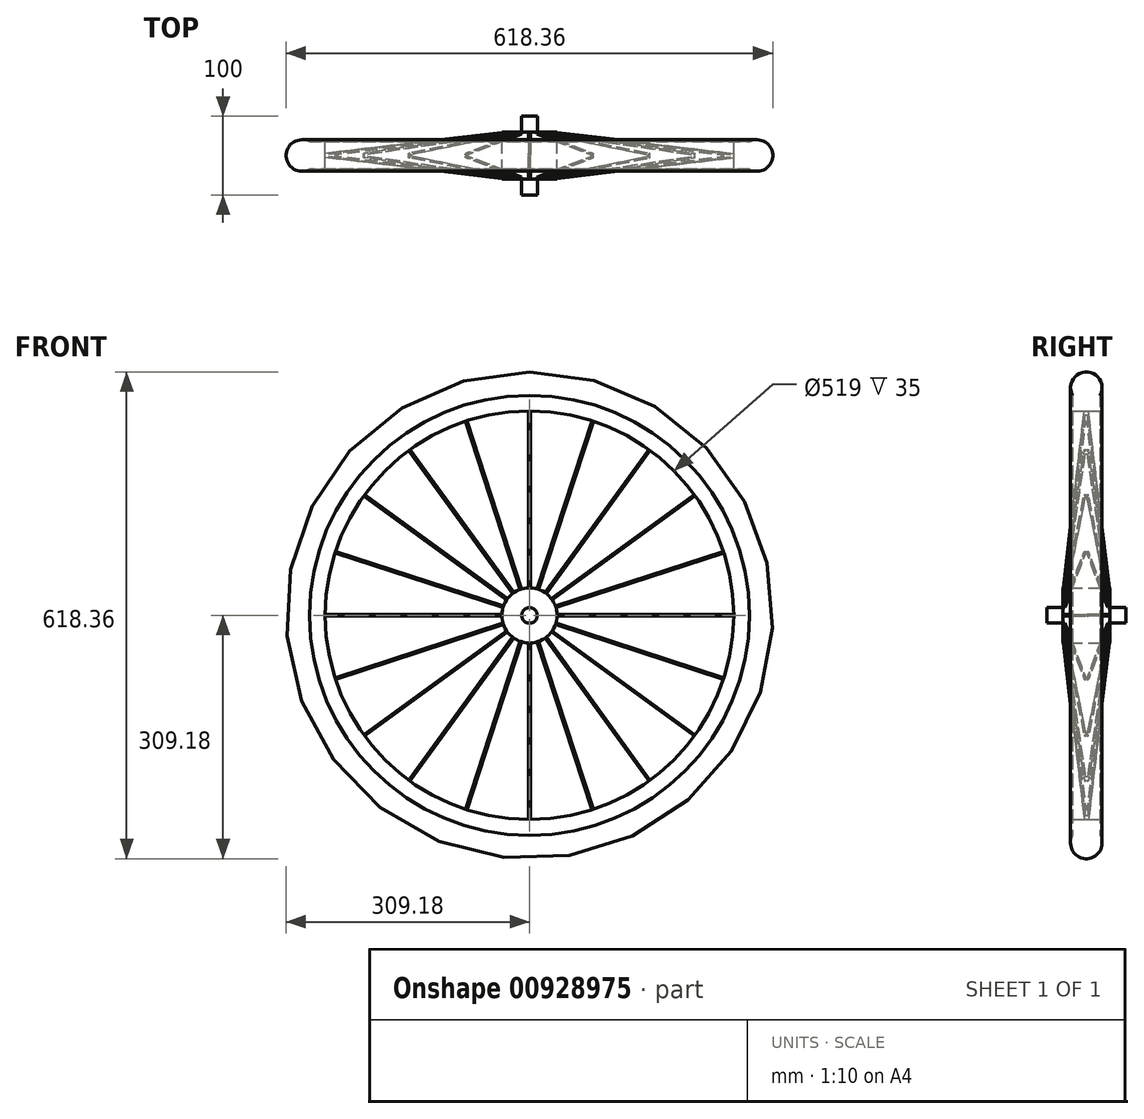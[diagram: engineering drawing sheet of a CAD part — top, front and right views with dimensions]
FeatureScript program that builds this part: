
annotation { "Feature Type Name" : "Feature", "Feature Type Description" : "" }
export const myFeature = defineFeature(function(context is Context, id is Id, definition is map)
    precondition{}
    {
        {
            var Q0;
            Q0=qCreatedBy(makeId("Front.planeOp"),FACE);
            var sketch = newSketch(context, id + "F0", { "sketchPlane" : qUnion([Q0])});
            skLineSegment(sketch, "E0.top", {"start": v(-17.5, 259.5) * mm, "end": v(17.5, 259.5) * mm});
            skLineSegment(sketch, "E0.left", {"start": v(-17.5, 279.5) * mm, "end": v(-17.5, 259.5) * mm});
            skLineSegment(sketch, "E0.right", {"start": v(17.5, 279.5) * mm, "end": v(17.5, 259.5) * mm});
            skArc(sketch, "E1", {"start": v(17.5, 279.5) * mm, "mid": v(0, 309.18) * mm, "end": v(-17.5, 279.5) * mm});
            skLineSegment(sketch, "E2.bottom", {"start": v(-30, 0) * mm, "end": v(30, 0) * mm});
            skLineSegment(sketch, "E2.top", {"start": v(-30, 35) * mm, "end": v(30, 35) * mm});
            skLineSegment(sketch, "E2.left", {"start": v(-30, 0) * mm, "end": v(-30, 35) * mm});
            skLineSegment(sketch, "E2.right", {"start": v(30, 0) * mm, "end": v(30, 35) * mm});
            skLineSegment(sketch, "E3.bottom", {"start": v(-30, 9.9) * mm, "end": v(-50, 9.9) * mm});
            skLineSegment(sketch, "E3.top", {"start": v(-30, 0) * mm, "end": v(-50, 0) * mm});
            skLineSegment(sketch, "E3.left", {"start": v(-30, 9.9) * mm, "end": v(-30, 0) * mm});
            skLineSegment(sketch, "E3.right", {"start": v(-50, 9.9) * mm, "end": v(-50, 0) * mm});
            skLineSegment(sketch, "E4.bottom", {"start": v(30, 9.9) * mm, "end": v(50, 9.9) * mm});
            skLineSegment(sketch, "E4.top", {"start": v(30, 0) * mm, "end": v(50, 0) * mm});
            skLineSegment(sketch, "E4.left", {"start": v(30, 9.9) * mm, "end": v(30, 0) * mm});
            skLineSegment(sketch, "E4.right", {"start": v(50, 9.9) * mm, "end": v(50, 0) * mm});
            skSolve(sketch);
        }
        {
            var Q0;
            Q0=makeQuery(id+"F0.imprint","IMPRINT",FACE,{"disambiguationData":[TD([[makeQuery(id+"F0.imprint","IMPRINT",EDGE,{"derivedFrom":sQuery(id+"F0.wireOp",EDGE,"E0.top")}),1.0]])]});
            var Q1;
            {var subQ1=sQuery(id+"F0.wireOp",EDGE,"E2.bottom");Q1=makeQuery(id+"F0.imprint","IMPRINT",FACE,{"disambiguationData":[TD([[makeQuery(id+"F0.imprint","IMPRINT",EDGE,{"derivedFrom":subQ1}),1.0]])]});}
            var Q2;
            {var subQ2=sQuery(id+"F0.wireOp",EDGE,"E4.bottom");Q2=makeQuery(id+"F0.imprint","IMPRINT",FACE,{"disambiguationData":[TD([[makeQuery(id+"F0.imprint","IMPRINT",EDGE,{"derivedFrom":subQ2}),-1.0]])]});}
            var Q3;
            {var subQ2=sQuery(id+"F0.wireOp",EDGE,"E3.bottom");Q3=makeQuery(id+"F0.imprint","IMPRINT",FACE,{"disambiguationData":[TD([[makeQuery(id+"F0.imprint","IMPRINT",EDGE,{"derivedFrom":subQ2}),1.0]])]});}
            var Q4;
            Q4=sQuery(id+"F0.wireOp",EDGE,"E2.bottom");
            revolve(context, id + "F1", {"surfaceOperationType" : NewSurfaceOperationType.NEW, "entities" : qUnion([Q0, Q1, Q2, Q3]), "axis" : qUnion([Q4]), "revolveType" : RevolveType.FULL});
        }
        {
            var Q0;
            Q0=qCreatedBy(makeId("Front.planeOp"),FACE);
            var sketch = newSketch(context, id + "F2", { "sketchPlane" : qUnion([Q0])});
            skLineSegment(sketch, "E5", {"start": v(29.79, 30.03) * mm, "end": v(0.16, 281.29) * mm});
            skLineSegment(sketch, "E6", {"start": v(29.79, 30.03) * mm, "end": v(27.79, 30.03) * mm});
            skLineSegment(sketch, "E7", {"start": v(0.16, 281.29) * mm, "end": v(-1.84, 281.29) * mm});
            skLineSegment(sketch, "E8", {"start": v(27.79, 30.03) * mm, "end": v(-1.84, 281.29) * mm});
            skLineSegment(sketch, "E9.MirrorCS", {"start": v(-29.79, 30.03) * mm, "end": v(-27.79, 30.03) * mm});
            skLineSegment(sketch, "E10.MirrorCS", {"start": v(-27.79, 30.03) * mm, "end": v(-0.72, 259.62) * mm});
            skLineSegment(sketch, "E11.MirrorCS", {"start": v(-0.16, 281.29) * mm, "end": v(-0.72, 259.62) * mm});
            skLineSegment(sketch, "E12.MirrorCS", {"start": v(-29.79, 30.03) * mm, "end": v(-0.16, 281.29) * mm});
            skSolve(sketch);
        }
        {
            var Q0;
            Q0=makeQuery(id+"F2.imprint","IMPRINT",FACE,{"disambiguationData":[TD([[makeQuery(id+"F2.imprint","IMPRINT",EDGE,{"derivedFrom":sQuery(id+"F2.wireOp",EDGE,"E5")}),1.0]])]});
            var Q1;
            Q1=makeQuery(id+"F2.imprint","IMPRINT",FACE,{"disambiguationData":[TD([[makeQuery(id+"F2.imprint","IMPRINT",EDGE,{"derivedFrom":sQuery(id+"F2.wireOp",EDGE,"E9.MirrorCS")}),1.0]])]});
            extrude(context, id + "F3", {"entities" : qUnion([Q0, Q1]), "operationType" : NewBodyOperationType.ADD, "endBound" : BoundingType.SYMMETRIC, "depth" : 2 * mm, "offsetDistance" : 25 * mm});
        }
        {
            var Q0;
            Q0=makeQuery(id+"F1.opRevolve","SWEPT_BODY",BODY,{"disambiguationData":[OSD([sQuery(id+"F0.wireOp",EDGE,"E0.top"),sQuery(id+"F0.wireOp",EDGE,"E0.left"),sQuery(id+"F0.wireOp",EDGE,"E0.right"),sQuery(id+"F0.wireOp",EDGE,"E1")])]});
            var Q1;
            Q1=makeQuery(id+"F1.opRevolve","SWEPT_EDGE",EDGE,{"disambiguationData":[OSD([sQuery(id+"F0.wireOp",EDGE,"E2.top"),sQuery(id+"F0.wireOp",EDGE,"E2.right")])]});
            circularPattern(context, id + "F4", {"operationType" : NewBodyOperationType.ADD, "entities" : qUnion([Q0]), "axis" : qUnion([Q1]), "angle" : 360 * degree, "instanceCount" : 20, "equalSpace" : true});
        }
        {
            var Q0;
            Q0=makeQuery(id+"F4.opPattern","COPY",BODY,{"derivedFrom":makeQuery(id+"F1.opRevolve","SWEPT_BODY",BODY,{"disambiguationData":[OSD([sQuery(id+"F0.wireOp",EDGE,"E0.top"),sQuery(id+"F0.wireOp",EDGE,"E0.left"),sQuery(id+"F0.wireOp",EDGE,"E0.right"),sQuery(id+"F0.wireOp",EDGE,"E1")])]}),"instanceName":"16"});
            var Q1;
            Q1=makeQuery(id+"F4.opPattern","COPY",BODY,{"derivedFrom":makeQuery(id+"F1.opRevolve","SWEPT_BODY",BODY,{"disambiguationData":[OSD([sQuery(id+"F0.wireOp",EDGE,"E0.top"),sQuery(id+"F0.wireOp",EDGE,"E0.left"),sQuery(id+"F0.wireOp",EDGE,"E0.right"),sQuery(id+"F0.wireOp",EDGE,"E1")])]}),"instanceName":"17"});
            var Q2;
            Q2=makeQuery(id+"F4.opPattern","COPY",BODY,{"derivedFrom":makeQuery(id+"F1.opRevolve","SWEPT_BODY",BODY,{"disambiguationData":[OSD([sQuery(id+"F0.wireOp",EDGE,"E0.top"),sQuery(id+"F0.wireOp",EDGE,"E0.left"),sQuery(id+"F0.wireOp",EDGE,"E0.right"),sQuery(id+"F0.wireOp",EDGE,"E1")])]}),"instanceName":"18"});
            var Q3;
            Q3=makeQuery(id+"F4.opPattern","COPY",BODY,{"derivedFrom":makeQuery(id+"F1.opRevolve","SWEPT_BODY",BODY,{"disambiguationData":[OSD([sQuery(id+"F0.wireOp",EDGE,"E0.top"),sQuery(id+"F0.wireOp",EDGE,"E0.left"),sQuery(id+"F0.wireOp",EDGE,"E0.right"),sQuery(id+"F0.wireOp",EDGE,"E1")])]}),"instanceName":"19"});
            var Q4;
            Q4=makeQuery(id+"F4.opPattern","COPY",BODY,{"derivedFrom":makeQuery(id+"F1.opRevolve","SWEPT_BODY",BODY,{"disambiguationData":[OSD([sQuery(id+"F0.wireOp",EDGE,"E0.top"),sQuery(id+"F0.wireOp",EDGE,"E0.left"),sQuery(id+"F0.wireOp",EDGE,"E0.right"),sQuery(id+"F0.wireOp",EDGE,"E1")])]}),"instanceName":"2"});
            var Q5;
            Q5=makeQuery(id+"F4.opPattern","COPY",BODY,{"derivedFrom":makeQuery(id+"F1.opRevolve","SWEPT_BODY",BODY,{"disambiguationData":[OSD([sQuery(id+"F0.wireOp",EDGE,"E0.top"),sQuery(id+"F0.wireOp",EDGE,"E0.left"),sQuery(id+"F0.wireOp",EDGE,"E0.right"),sQuery(id+"F0.wireOp",EDGE,"E1")])]}),"instanceName":"1"});
            var Q6;
            Q6=makeQuery(id+"F4.opPattern","COPY",BODY,{"derivedFrom":makeQuery(id+"F1.opRevolve","SWEPT_BODY",BODY,{"disambiguationData":[OSD([sQuery(id+"F0.wireOp",EDGE,"E0.top"),sQuery(id+"F0.wireOp",EDGE,"E0.left"),sQuery(id+"F0.wireOp",EDGE,"E0.right"),sQuery(id+"F0.wireOp",EDGE,"E1")])]}),"instanceName":"9"});
            var Q7;
            Q7=makeQuery(id+"F4.opPattern","COPY",BODY,{"derivedFrom":makeQuery(id+"F1.opRevolve","SWEPT_BODY",BODY,{"disambiguationData":[OSD([sQuery(id+"F0.wireOp",EDGE,"E0.top"),sQuery(id+"F0.wireOp",EDGE,"E0.left"),sQuery(id+"F0.wireOp",EDGE,"E0.right"),sQuery(id+"F0.wireOp",EDGE,"E1")])]}),"instanceName":"12"});
            var Q8;
            Q8=makeQuery(id+"F4.opPattern","COPY",BODY,{"derivedFrom":makeQuery(id+"F1.opRevolve","SWEPT_BODY",BODY,{"disambiguationData":[OSD([sQuery(id+"F0.wireOp",EDGE,"E0.top"),sQuery(id+"F0.wireOp",EDGE,"E0.left"),sQuery(id+"F0.wireOp",EDGE,"E0.right"),sQuery(id+"F0.wireOp",EDGE,"E1")])]}),"instanceName":"11"});
            var Q9;
            Q9=makeQuery(id+"F4.opPattern","COPY",BODY,{"derivedFrom":makeQuery(id+"F1.opRevolve","SWEPT_BODY",BODY,{"disambiguationData":[OSD([sQuery(id+"F0.wireOp",EDGE,"E0.top"),sQuery(id+"F0.wireOp",EDGE,"E0.left"),sQuery(id+"F0.wireOp",EDGE,"E0.right"),sQuery(id+"F0.wireOp",EDGE,"E1")])]}),"instanceName":"10"});
            var Q10;
            Q10=makeQuery(id+"F4.opPattern","COPY",BODY,{"derivedFrom":makeQuery(id+"F1.opRevolve","SWEPT_BODY",BODY,{"disambiguationData":[OSD([sQuery(id+"F0.wireOp",EDGE,"E0.top"),sQuery(id+"F0.wireOp",EDGE,"E0.left"),sQuery(id+"F0.wireOp",EDGE,"E0.right"),sQuery(id+"F0.wireOp",EDGE,"E1")])]}),"instanceName":"3"});
            var Q11;
            Q11=makeQuery(id+"F4.opPattern","COPY",BODY,{"derivedFrom":makeQuery(id+"F1.opRevolve","SWEPT_BODY",BODY,{"disambiguationData":[OSD([sQuery(id+"F0.wireOp",EDGE,"E0.top"),sQuery(id+"F0.wireOp",EDGE,"E0.left"),sQuery(id+"F0.wireOp",EDGE,"E0.right"),sQuery(id+"F0.wireOp",EDGE,"E1")])]}),"instanceName":"4"});
            var Q12;
            Q12=makeQuery(id+"F1.opRevolve","SWEPT_BODY",BODY,{"disambiguationData":[OSD([sQuery(id+"F0.wireOp",EDGE,"E0.top"),sQuery(id+"F0.wireOp",EDGE,"E0.left"),sQuery(id+"F0.wireOp",EDGE,"E0.right"),sQuery(id+"F0.wireOp",EDGE,"E1")])]});
            var Q13;
            Q13=makeQuery(id+"F4.opPattern","COPY",BODY,{"derivedFrom":makeQuery(id+"F1.opRevolve","SWEPT_BODY",BODY,{"disambiguationData":[OSD([sQuery(id+"F0.wireOp",EDGE,"E0.top"),sQuery(id+"F0.wireOp",EDGE,"E0.left"),sQuery(id+"F0.wireOp",EDGE,"E0.right"),sQuery(id+"F0.wireOp",EDGE,"E1")])]}),"instanceName":"5"});
            var Q14;
            Q14=makeQuery(id+"F4.opPattern","COPY",BODY,{"derivedFrom":makeQuery(id+"F1.opRevolve","SWEPT_BODY",BODY,{"disambiguationData":[OSD([sQuery(id+"F0.wireOp",EDGE,"E0.top"),sQuery(id+"F0.wireOp",EDGE,"E0.left"),sQuery(id+"F0.wireOp",EDGE,"E0.right"),sQuery(id+"F0.wireOp",EDGE,"E1")])]}),"instanceName":"6"});
            var Q15;
            Q15=makeQuery(id+"F4.opPattern","COPY",BODY,{"derivedFrom":makeQuery(id+"F1.opRevolve","SWEPT_BODY",BODY,{"disambiguationData":[OSD([sQuery(id+"F0.wireOp",EDGE,"E0.top"),sQuery(id+"F0.wireOp",EDGE,"E0.left"),sQuery(id+"F0.wireOp",EDGE,"E0.right"),sQuery(id+"F0.wireOp",EDGE,"E1")])]}),"instanceName":"7"});
            var Q16;
            Q16=makeQuery(id+"F4.opPattern","COPY",BODY,{"derivedFrom":makeQuery(id+"F1.opRevolve","SWEPT_BODY",BODY,{"disambiguationData":[OSD([sQuery(id+"F0.wireOp",EDGE,"E0.top"),sQuery(id+"F0.wireOp",EDGE,"E0.left"),sQuery(id+"F0.wireOp",EDGE,"E0.right"),sQuery(id+"F0.wireOp",EDGE,"E1")])]}),"instanceName":"8"});
            var Q17;
            Q17=makeQuery(id+"F4.opPattern","COPY",BODY,{"derivedFrom":makeQuery(id+"F1.opRevolve","SWEPT_BODY",BODY,{"disambiguationData":[OSD([sQuery(id+"F0.wireOp",EDGE,"E0.top"),sQuery(id+"F0.wireOp",EDGE,"E0.left"),sQuery(id+"F0.wireOp",EDGE,"E0.right"),sQuery(id+"F0.wireOp",EDGE,"E1")])]}),"instanceName":"13"});
            var Q18;
            Q18=makeQuery(id+"F4.opPattern","COPY",BODY,{"derivedFrom":makeQuery(id+"F1.opRevolve","SWEPT_BODY",BODY,{"disambiguationData":[OSD([sQuery(id+"F0.wireOp",EDGE,"E0.top"),sQuery(id+"F0.wireOp",EDGE,"E0.left"),sQuery(id+"F0.wireOp",EDGE,"E0.right"),sQuery(id+"F0.wireOp",EDGE,"E1")])]}),"instanceName":"15"});
            var Q19;
            Q19=makeQuery(id+"F4.opPattern","COPY",BODY,{"derivedFrom":makeQuery(id+"F1.opRevolve","SWEPT_BODY",BODY,{"disambiguationData":[OSD([sQuery(id+"F0.wireOp",EDGE,"E0.top"),sQuery(id+"F0.wireOp",EDGE,"E0.left"),sQuery(id+"F0.wireOp",EDGE,"E0.right"),sQuery(id+"F0.wireOp",EDGE,"E1")])]}),"instanceName":"14"});
            var Q20;
            Q20=makeQuery(id+"F1.opRevolve","SWEPT_BODY",BODY,{"disambiguationData":[OSD([sQuery(id+"F0.wireOp",EDGE,"E2.bottom"),sQuery(id+"F0.wireOp",EDGE,"E2.top"),sQuery(id+"F0.wireOp",EDGE,"E2.left"),sQuery(id+"F0.wireOp",EDGE,"E2.right"),sQuery(id+"F0.wireOp",EDGE,"E3.bottom"),sQuery(id+"F0.wireOp",EDGE,"E3.top"),sQuery(id+"F0.wireOp",EDGE,"E3.right"),sQuery(id+"F0.wireOp",EDGE,"E4.bottom"),sQuery(id+"F0.wireOp",EDGE,"E4.top"),sQuery(id+"F0.wireOp",EDGE,"E4.right")])]});
            var Q21;
            Q21=makeQuery(id+"F3.opExtrude","SWEPT_BODY",BODY,{"disambiguationData":[OSD([sQuery(id+"F0.wireOp",EDGE,"E3.bottom"),sQuery(id+"F0.wireOp",EDGE,"E3.top"),sQuery(id+"F0.wireOp",EDGE,"E3.left"),sQuery(id+"F0.wireOp",EDGE,"E3.right")])]});
            var Q22;
            Q22=makeQuery(id+"F3.opExtrude","SWEPT_BODY",BODY,{"disambiguationData":[OSD([sQuery(id+"F0.wireOp",EDGE,"E4.bottom"),sQuery(id+"F0.wireOp",EDGE,"E4.top"),sQuery(id+"F0.wireOp",EDGE,"E4.left"),sQuery(id+"F0.wireOp",EDGE,"E4.right")])]});
            var Q23;
            Q23=sQuery(id+"F0.wireOp",EDGE,"E0.right");
            transform(context, id + "F5", {"entities" : qUnion([Q0, Q1, Q2, Q3, Q4, Q5, Q6, Q7, Q8, Q9, Q10, Q11, Q12, Q13, Q14, Q15, Q16, Q17, Q18, Q19, Q20, Q21, Q22]), "transformType" : TransformType.ROTATION, "transformAxis" : qUnion([Q23]), "angle" : 90 * degree, "makeCopy" : false});
        }
    });
